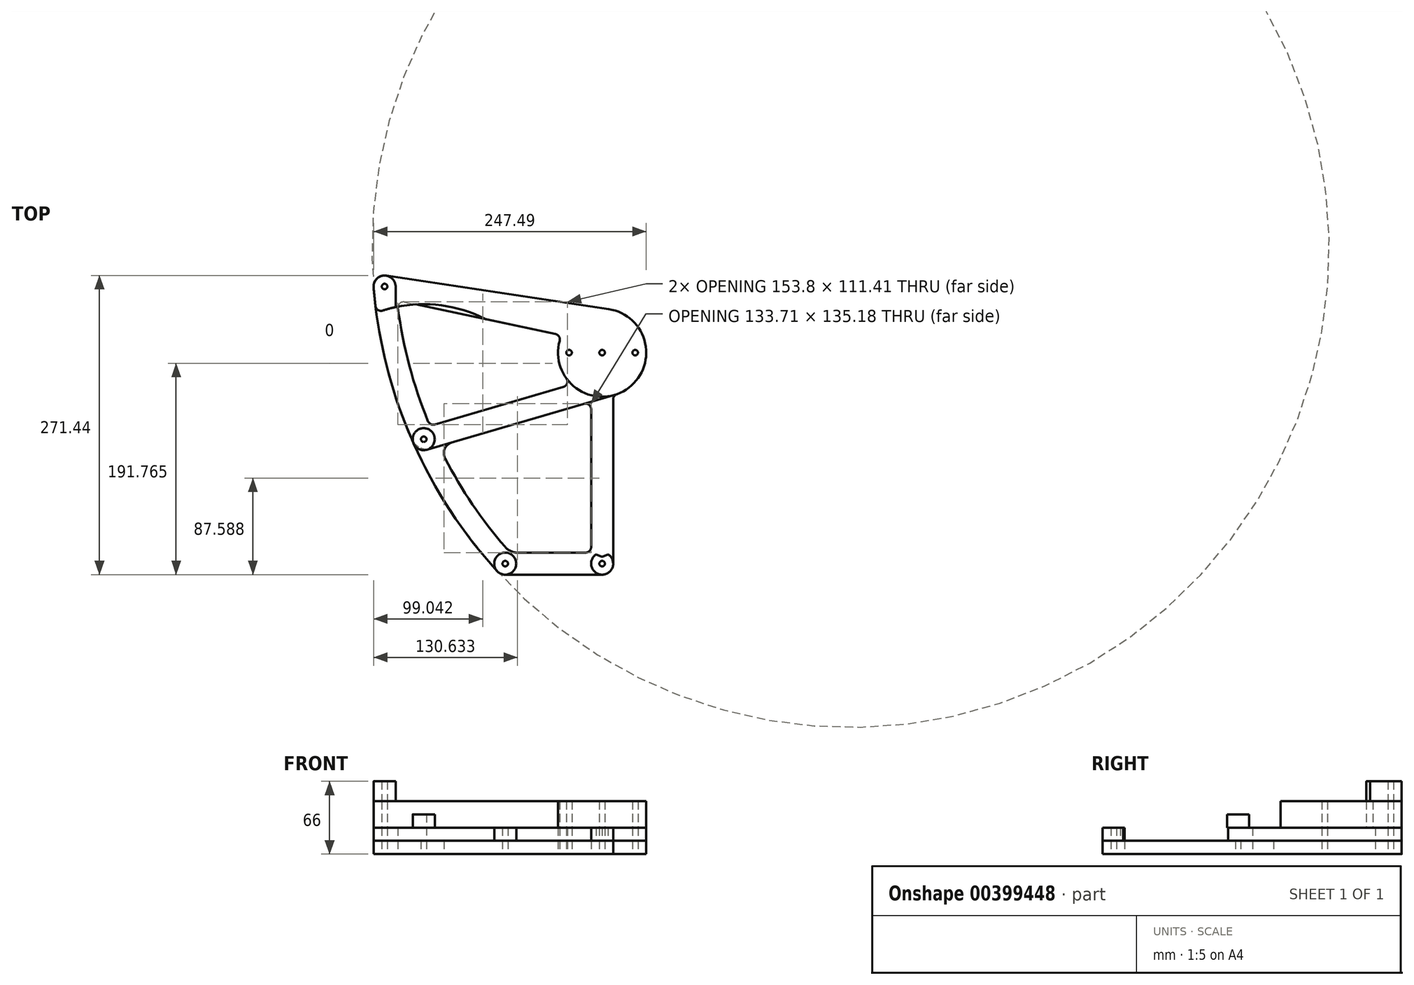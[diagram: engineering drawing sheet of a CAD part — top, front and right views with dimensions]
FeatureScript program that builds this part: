
annotation { "Feature Type Name" : "Feature", "Feature Type Description" : "" }
export const myFeature = defineFeature(function(context is Context, id is Id, definition is map)
    precondition{}
    {
        {
            var Q0;
            Q0=qCreatedBy(makeId("Top.planeOp"),FACE);
            var sketch = newSketch(context, id + "F0", { "sketchPlane" : qUnion([Q0])});
            skArc(sketch, "E0", {"start": v(-38.57, 10.6) * mm, "mid": v(-39.37, -7.07) * mm, "end": v(-32.47, -23.36) * mm});
            skCircle(sketch, "E1", {"center": v(0, 0) * mm, "radius": 2.5 * mm});
            skCircle(sketch, "E2", {"center": v(-30, 0) * mm, "radius": 2.5 * mm});
            skCircle(sketch, "E3", {"center": v(30, 0) * mm, "radius": 2.5 * mm});
            skCircle(sketch, "E4", {"center": v(-197.49, 60) * mm, "radius": 2.5 * mm});
            skCircle(sketch, "E5", {"center": v(-161.97, -78.52) * mm, "radius": 2.5 * mm});
            skCircle(sketch, "E6", {"center": v(-88, -191.44) * mm, "radius": 2.5 * mm});
            skCircle(sketch, "E7", {"center": v(0, -191.44) * mm, "radius": 2.5 * mm});
            skCircle(sketch, "E8", {"center": v(-197.49, 60) * mm, "radius": 10 * mm, "construction": true});
            skCircle(sketch, "E9", {"center": v(-161.97, -78.52) * mm, "radius": 10 * mm, "construction": true});
            skCircle(sketch, "E10", {"center": v(-88, -191.44) * mm, "radius": 10 * mm, "construction": true});
            skArc(sketch, "E11", {"start": v(0, -201.44) * mm, "mid": v(7.07, -198.51) * mm, "end": v(10, -191.44) * mm});
            skLineSegment(sketch, "E12", {"start": v(-196, 69.89) * mm, "end": v(5.94, 39.56) * mm});
            skLineSegment(sketch, "E13", {"start": v(-88, -201.44) * mm, "end": v(0, -201.44) * mm});
            skLineSegment(sketch, "E14", {"start": v(10, -191.44) * mm, "end": v(10, -42.43) * mm});
            skLineSegment(sketch, "E15", {"start": v(-10, -51.25) * mm, "end": v(-10, -176.44) * mm});
            skLineSegment(sketch, "E16", {"start": v(-15, -181.44) * mm, "end": v(-76.76, -181.44) * mm});
            skArc(sketch, "E17", {"start": v(-207.45, 59.18) * mm, "mid": v(-172.78, -78.8) * mm, "end": v(-95.38, -198.18) * mm});
            skPoint(sketch, "E17.first.point", {"position": v(-207.45, 59.18) * mm});
            skPoint(sketch, "E17.second.point", {"position": v(-171.1, -82.6) * mm});
            skPoint(sketch, "E17.third.point", {"position": v(-95.38, -198.18) * mm});
            skArc(sketch, "E18", {"start": v(-185.33, 40.38) * mm, "mid": v(-175, -11.84) * mm, "end": v(-158.04, -62.29) * mm});
            skPoint(sketch, "E18.first.point", {"position": v(-188.38, 55.87) * mm});
            skPoint(sketch, "E18.second.point", {"position": v(-152.84, -74.44) * mm});
            skPoint(sketch, "E18.third.point", {"position": v(-85.08, -181.88) * mm});
            skLineSegment(sketch, "E19", {"start": v(-179.34, 45.92) * mm, "end": v(-42.35, 16.82) * mm});
            skLineSegment(sketch, "E20", {"start": v(-136.52, -81.5) * mm, "end": v(-16.4, -46.45) * mm});
            skLineSegment(sketch, "E21", {"start": v(-152.01, -65.2) * mm, "end": v(-35.12, -31.08) * mm});
            skArc(sketch, "E22", {"start": v(-95.38, -198.18) * mm, "mid": v(-92.03, -200.6) * mm, "end": v(-88, -201.44) * mm});
            skArc(sketch, "E23.filletArc", {"start": v(-88.1, -176.25) * mm, "mid": v(-83, -180.08) * mm, "end": v(-76.76, -181.44) * mm});
            skArc(sketch, "E24.trimOffspring", {"start": v(-142.6, -95.7) * mm, "mid": v(-117.73, -137.58) * mm, "end": v(-88.1, -176.25) * mm});
            skArc(sketch, "E25.filletArc", {"start": v(-158.04, -62.29) * mm, "mid": v(-155.58, -64.9) * mm, "end": v(-152.01, -65.2) * mm});
            skArc(sketch, "E26.filletArc", {"start": v(-136.52, -81.5) * mm, "mid": v(-142.91, -87.17) * mm, "end": v(-142.6, -95.7) * mm});
            skArc(sketch, "E27.filletArc", {"start": v(-179.34, 45.92) * mm, "mid": v(-183.77, 44.7) * mm, "end": v(-185.33, 40.38) * mm});
            skArc(sketch, "E28.trimOffspring", {"start": v(13.33, -37.71) * mm, "mid": v(39.82, 3.8) * mm, "end": v(5.94, 39.56) * mm});
            skPoint(sketch, "E29.visualSharp", {"position": v(-36.81, 15.64) * mm});
            skArc(sketch, "E29.filletArc", {"start": v(-38.57, 10.6) * mm, "mid": v(-39.12, 14.53) * mm, "end": v(-42.35, 16.82) * mm});
            skPoint(sketch, "E30.visualSharp", {"position": v(-27.65, -28.9) * mm});
            skArc(sketch, "E30.filletArc", {"start": v(-35.12, -31.08) * mm, "mid": v(-31.8, -27.91) * mm, "end": v(-32.47, -23.36) * mm});
            skPoint(sketch, "E31.visualSharp", {"position": v(10, -38.73) * mm});
            skArc(sketch, "E31.filletArc", {"start": v(13.33, -37.71) * mm, "mid": v(10.92, -39.54) * mm, "end": v(10, -42.43) * mm});
            skPoint(sketch, "E32.newPointB", {"position": v(0, -41.67) * mm});
            skArc(sketch, "E32.filletArc", {"start": v(-10, -51.25) * mm, "mid": v(-12, -47.25) * mm, "end": v(-16.4, -46.45) * mm});
            skArc(sketch, "E33", {"start": v(-207.45, 59.18) * mm, "mid": v(-204.32, 67.3) * mm, "end": v(-196, 69.89) * mm});
            skPoint(sketch, "E34.visualSharp", {"position": v(-10, -181.44) * mm});
            skArc(sketch, "E34.filletArc", {"start": v(-15, -181.44) * mm, "mid": v(-11.46, -179.98) * mm, "end": v(-10, -176.44) * mm});
            skSolve(sketch);
        }
        {
            var Q0;
            Q0=makeQuery(id+"F0.imprint","IMPRINT",FACE,{"disambiguationData":[TD([[makeQuery(id+"F0.imprint","IMPRINT",EDGE,{"derivedFrom":sQuery(id+"F0.wireOp",EDGE,"E0")}),1.0]])]});
            extrude(context, id + "F1", {"entities" : qUnion([Q0]), "depth" : 12 * mm});
        }
        {
            var Q0;
            Q0=makeQuery(id+"F1.opExtrude","CAP_FACE",FACE,{"disambiguationData":[OSD([sQuery(id+"F0.wireOp",EDGE,"E0"),sQuery(id+"F0.wireOp",EDGE,"E1"),sQuery(id+"F0.wireOp",EDGE,"E2"),sQuery(id+"F0.wireOp",EDGE,"E3"),sQuery(id+"F0.wireOp",EDGE,"E4"),sQuery(id+"F0.wireOp",EDGE,"E5"),sQuery(id+"F0.wireOp",EDGE,"E6"),sQuery(id+"F0.wireOp",EDGE,"E7"),sQuery(id+"F0.wireOp",EDGE,"E11"),sQuery(id+"F0.wireOp",EDGE,"E12"),sQuery(id+"F0.wireOp",EDGE,"E13"),sQuery(id+"F0.wireOp",EDGE,"E14"),sQuery(id+"F0.wireOp",EDGE,"E15"),sQuery(id+"F0.wireOp",EDGE,"E16"),sQuery(id+"F0.wireOp",EDGE,"E17"),sQuery(id+"F0.wireOp",EDGE,"E18"),sQuery(id+"F0.wireOp",EDGE,"E19"),sQuery(id+"F0.wireOp",EDGE,"E20"),sQuery(id+"F0.wireOp",EDGE,"E21"),sQuery(id+"F0.wireOp",EDGE,"E22"),sQuery(id+"F0.wireOp",EDGE,"E23.filletArc"),sQuery(id+"F0.wireOp",EDGE,"E24.trimOffspring"),sQuery(id+"F0.wireOp",EDGE,"E25.filletArc"),sQuery(id+"F0.wireOp",EDGE,"E26.filletArc"),sQuery(id+"F0.wireOp",EDGE,"E27.filletArc"),sQuery(id+"F0.wireOp",EDGE,"E28.trimOffspring"),sQuery(id+"F0.wireOp",EDGE,"E29.filletArc"),sQuery(id+"F0.wireOp",EDGE,"E30.filletArc"),sQuery(id+"F0.wireOp",EDGE,"E31.filletArc"),sQuery(id+"F0.wireOp",EDGE,"E32.filletArc"),sQuery(id+"F0.wireOp",EDGE,"E33"),sQuery(id+"F0.wireOp",EDGE,"E34.filletArc")])],"isStart":false});
            var sketch = newSketch(context, id + "F2", { "sketchPlane" : qUnion([Q0])});
            skArc(sketch, "E35.0", {"start": v(-207.45, 59.18) * mm, "mid": v(-204.32, 67.3) * mm, "end": v(-196, 69.89) * mm});
            skLineSegment(sketch, "E35.1", {"start": v(-196, 69.89) * mm, "end": v(5.94, 39.56) * mm});
            skArc(sketch, "E35.2", {"start": v(-207.45, 59.18) * mm, "mid": v(-195.85, -11.06) * mm, "end": v(-172.92, -78.47) * mm});
            skLineSegment(sketch, "E35.3", {"start": v(-154.96, -86.9) * mm, "end": v(11.2, -38.4) * mm});
            skArc(sketch, "E35.4", {"start": v(11.2, -38.4) * mm, "mid": v(39.9, 2.7) * mm, "end": v(5.94, 39.56) * mm});
            skPoint(sketch, "E36.orphan", {"position": v(-136.52, -81.5) * mm});
            skPoint(sketch, "E37.orphan", {"position": v(-16.4, -46.45) * mm});
            skPoint(sketch, "E38.orphan", {"position": v(13.33, -37.71) * mm});
            skPoint(sketch, "E39.orphan", {"position": v(-95.38, -198.18) * mm});
            skPoint(sketch, "E40.visualSharp", {"position": v(-167.46, -90.54) * mm});
            skArc(sketch, "E40.filletArc", {"start": v(-172.92, -78.47) * mm, "mid": v(-165.53, -86.07) * mm, "end": v(-154.96, -86.9) * mm});
            skArc(sketch, "E41.0", {"start": v(-185.33, 40.38) * mm, "mid": v(-175, -11.84) * mm, "end": v(-158.04, -62.29) * mm});
            skArc(sketch, "E41.1", {"start": v(-179.34, 45.92) * mm, "mid": v(-183.77, 44.7) * mm, "end": v(-185.33, 40.38) * mm});
            skLineSegment(sketch, "E41.2", {"start": v(-179.34, 45.92) * mm, "end": v(-42.35, 16.82) * mm});
            skArc(sketch, "E41.3", {"start": v(-38.57, 10.6) * mm, "mid": v(-39.12, 14.53) * mm, "end": v(-42.35, 16.82) * mm});
            skArc(sketch, "E41.4", {"start": v(-38.57, 10.6) * mm, "mid": v(-39.37, -7.07) * mm, "end": v(-32.47, -23.36) * mm});
            skArc(sketch, "E41.5", {"start": v(-35.12, -31.08) * mm, "mid": v(-31.8, -27.91) * mm, "end": v(-32.47, -23.36) * mm});
            skLineSegment(sketch, "E41.6", {"start": v(-152.01, -65.2) * mm, "end": v(-35.12, -31.08) * mm});
            skArc(sketch, "E41.7", {"start": v(-158.04, -62.29) * mm, "mid": v(-155.58, -64.9) * mm, "end": v(-152.01, -65.2) * mm});
            skCircle(sketch, "E42.0", {"center": v(-197.49, 60) * mm, "radius": 2.5 * mm});
            skCircle(sketch, "E43.1", {"center": v(-161.97, -78.52) * mm, "radius": 2.5 * mm});
            skCircle(sketch, "E44.0", {"center": v(30, 0) * mm, "radius": 2.5 * mm});
            skCircle(sketch, "E45.0", {"center": v(-30, 0) * mm, "radius": 2.5 * mm});
            skCircle(sketch, "E45.1", {"center": v(0, 0) * mm, "radius": 2.5 * mm});
            skSolve(sketch);
        }
        {
            var Q0;
            Q0 = qSketchRegion(id + "F2", true);
            extrude(context, id + "F3", {"entities" : qUnion([Q0]), "depth" : 12 * mm});
        }
        {
            var Q0;
            Q0=makeQuery(id+"F3.opExtrude","CAP_FACE",FACE,{"disambiguationData":[OSD([sQuery(id+"F2.wireOp",EDGE,"E35.0"),sQuery(id+"F2.wireOp",EDGE,"E35.1"),sQuery(id+"F2.wireOp",EDGE,"E35.2"),sQuery(id+"F2.wireOp",EDGE,"E35.3"),sQuery(id+"F2.wireOp",EDGE,"E35.4"),sQuery(id+"F2.wireOp",EDGE,"E40.filletArc"),sQuery(id+"F2.wireOp",EDGE,"E41.0"),sQuery(id+"F2.wireOp",EDGE,"E41.1"),sQuery(id+"F2.wireOp",EDGE,"E41.2"),sQuery(id+"F2.wireOp",EDGE,"E41.3"),sQuery(id+"F2.wireOp",EDGE,"E41.4"),sQuery(id+"F2.wireOp",EDGE,"E41.5"),sQuery(id+"F2.wireOp",EDGE,"E41.6"),sQuery(id+"F2.wireOp",EDGE,"E41.7"),sQuery(id+"F2.wireOp",EDGE,"E42.0"),sQuery(id+"F2.wireOp",EDGE,"E43.1"),sQuery(id+"F2.wireOp",EDGE,"E44.0"),sQuery(id+"F2.wireOp",EDGE,"E45.0"),sQuery(id+"F2.wireOp",EDGE,"E45.1")])],"isStart":false});
            var sketch = newSketch(context, id + "F4", { "sketchPlane" : qUnion([Q0])});
            skCircle(sketch, "E46.0", {"center": v(-161.97, -78.52) * mm, "radius": 2.5 * mm, "construction": true});
            skArc(sketch, "E47", {"start": v(-106.23, 30.57) * mm, "mid": v(-152, 43.57) * mm, "end": v(-199.26, 38.17) * mm});
            skArc(sketch, "E48.0", {"start": v(-207.45, 59.18) * mm, "mid": v(-204.32, 67.3) * mm, "end": v(-196, 69.89) * mm});
            skArc(sketch, "E48.1", {"start": v(-207.45, 59.18) * mm, "mid": v(-206.68, 50.75) * mm, "end": v(-205.74, 42.33) * mm});
            skLineSegment(sketch, "E49.0", {"start": v(-196, 69.89) * mm, "end": v(5.94, 39.56) * mm});
            skArc(sketch, "E50.converted", {"start": v(-38.57, 10.6) * mm, "mid": v(21.81, -33.53) * mm, "end": v(5.94, 39.56) * mm});
            skPoint(sketch, "E51.orphan", {"position": v(11.2, -38.4) * mm});
            skLineSegment(sketch, "E52.0", {"start": v(-105, 30.13) * mm, "end": v(-42.35, 16.82) * mm});
            skArc(sketch, "E53.0", {"start": v(-38.57, 10.6) * mm, "mid": v(-39.12, 14.53) * mm, "end": v(-42.35, 16.82) * mm});
            skPoint(sketch, "E54.orphan", {"position": v(-172.92, -78.47) * mm});
            skPoint(sketch, "E55.orphan", {"position": v(-179.34, 45.92) * mm});
            skCircle(sketch, "E56.0", {"center": v(-30, 0) * mm, "radius": 2.5 * mm});
            skCircle(sketch, "E56.1", {"center": v(0, 0) * mm, "radius": 2.5 * mm});
            skCircle(sketch, "E56.2", {"center": v(30, 0) * mm, "radius": 2.5 * mm});
            skPoint(sketch, "E57.visualSharp", {"position": v(-204.95, 36.2) * mm});
            skArc(sketch, "E57.filletArc", {"start": v(-205.74, 42.33) * mm, "mid": v(-203.48, 38.72) * mm, "end": v(-199.26, 38.17) * mm});
            skPoint(sketch, "E58.visualSharp", {"position": v(-105.65, 30.27) * mm});
            skArc(sketch, "E58.filletArc", {"start": v(-106.23, 30.57) * mm, "mid": v(-105.63, 30.3) * mm, "end": v(-105, 30.13) * mm});
            skCircle(sketch, "E59.0", {"center": v(-197.49, 60) * mm, "radius": 2.5 * mm});
            skSolve(sketch);
        }
        {
            var Q0;
            Q0 = qSketchRegion(id + "F4", true);
            extrude(context, id + "F5", {"entities" : qUnion([Q0]), "depth" : 24 * mm});
        }
        {
            var Q0;
            Q0=makeQuery(id+"F1.opExtrude","CAP_FACE",FACE,{"disambiguationData":[OSD([sQuery(id+"F0.wireOp",EDGE,"E0"),sQuery(id+"F0.wireOp",EDGE,"E1"),sQuery(id+"F0.wireOp",EDGE,"E2"),sQuery(id+"F0.wireOp",EDGE,"E3"),sQuery(id+"F0.wireOp",EDGE,"E4"),sQuery(id+"F0.wireOp",EDGE,"E5"),sQuery(id+"F0.wireOp",EDGE,"E6"),sQuery(id+"F0.wireOp",EDGE,"E7"),sQuery(id+"F0.wireOp",EDGE,"E11"),sQuery(id+"F0.wireOp",EDGE,"E12"),sQuery(id+"F0.wireOp",EDGE,"E13"),sQuery(id+"F0.wireOp",EDGE,"E14"),sQuery(id+"F0.wireOp",EDGE,"E15"),sQuery(id+"F0.wireOp",EDGE,"E16"),sQuery(id+"F0.wireOp",EDGE,"E17"),sQuery(id+"F0.wireOp",EDGE,"E18"),sQuery(id+"F0.wireOp",EDGE,"E19"),sQuery(id+"F0.wireOp",EDGE,"E20"),sQuery(id+"F0.wireOp",EDGE,"E21"),sQuery(id+"F0.wireOp",EDGE,"E22"),sQuery(id+"F0.wireOp",EDGE,"E23.filletArc"),sQuery(id+"F0.wireOp",EDGE,"E24.trimOffspring"),sQuery(id+"F0.wireOp",EDGE,"E25.filletArc"),sQuery(id+"F0.wireOp",EDGE,"E26.filletArc"),sQuery(id+"F0.wireOp",EDGE,"E27.filletArc"),sQuery(id+"F0.wireOp",EDGE,"E28.trimOffspring"),sQuery(id+"F0.wireOp",EDGE,"E29.filletArc"),sQuery(id+"F0.wireOp",EDGE,"E30.filletArc"),sQuery(id+"F0.wireOp",EDGE,"E31.filletArc"),sQuery(id+"F0.wireOp",EDGE,"E32.filletArc"),sQuery(id+"F0.wireOp",EDGE,"E33"),sQuery(id+"F0.wireOp",EDGE,"E34.filletArc")])],"isStart":false});
            var sketch = newSketch(context, id + "F6", { "sketchPlane" : qUnion([Q0])});
            skCircle(sketch, "E60.0", {"center": v(-88, -191.44) * mm, "radius": 2.5 * mm});
            skCircle(sketch, "E60.1", {"center": v(0, -191.44) * mm, "radius": 2.5 * mm});
            skArc(sketch, "E61", {"start": v(-5.3, -182.97) * mm, "mid": v(0, -201.44) * mm, "end": v(5.3, -182.97) * mm});
            skCircle(sketch, "E62", {"center": v(-88, -191.44) * mm, "radius": 10 * mm});
            skLineSegment(sketch, "E63", {"start": v(0, -191.44) * mm, "end": v(0, -113.22) * mm, "construction": true});
            skLineSegment(sketch, "E64", {"start": v(-5.3, -182.97) * mm, "end": v(0, -185.44) * mm});
            skLineSegment(sketch, "E65", {"start": v(0, -185.44) * mm, "end": v(5.3, -182.97) * mm});
            skSolve(sketch);
        }
        {
            var Q0;
            Q0 = qSketchRegion(id + "F6", true);
            extrude(context, id + "F7", {"entities" : qUnion([Q0]), "depth" : 12 * mm});
        }
        {
            var Q0;
            Q0=makeQuery(id+"F5.opExtrude","CAP_FACE",FACE,{"disambiguationData":[OSD([sQuery(id+"F4.wireOp",EDGE,"E47"),sQuery(id+"F4.wireOp",EDGE,"E48.0"),sQuery(id+"F4.wireOp",EDGE,"E48.1"),sQuery(id+"F4.wireOp",EDGE,"E49.0"),sQuery(id+"F4.wireOp",EDGE,"E50.converted"),sQuery(id+"F4.wireOp",EDGE,"E52.0"),sQuery(id+"F4.wireOp",EDGE,"E53.0"),sQuery(id+"F4.wireOp",EDGE,"E56.0"),sQuery(id+"F4.wireOp",EDGE,"E56.1"),sQuery(id+"F4.wireOp",EDGE,"E56.2"),sQuery(id+"F4.wireOp",EDGE,"E57.filletArc"),sQuery(id+"F4.wireOp",EDGE,"E58.filletArc"),sQuery(id+"F4.wireOp",EDGE,"E59.0")])],"isStart":false});
            var sketch = newSketch(context, id + "F8", { "sketchPlane" : qUnion([Q0])});
            skCircle(sketch, "E66.0", {"center": v(-197.49, 60) * mm, "radius": 2.5 * mm});
            skArc(sketch, "E67.0", {"start": v(-207.45, 59.18) * mm, "mid": v(-197.94, 69.99) * mm, "end": v(-187.49, 60.09) * mm});
            skArc(sketch, "E68.0", {"start": v(-207.45, 59.18) * mm, "mid": v(-206.68, 50.75) * mm, "end": v(-205.74, 42.33) * mm});
            skArc(sketch, "E69.0", {"start": v(-205.74, 42.33) * mm, "mid": v(-203.48, 38.72) * mm, "end": v(-199.26, 38.17) * mm});
            skArc(sketch, "E70.0", {"start": v(-187.49, 41.3) * mm, "mid": v(-193.41, 39.88) * mm, "end": v(-199.26, 38.17) * mm});
            skPoint(sketch, "E71.orphan", {"position": v(-196, 69.89) * mm});
            skPoint(sketch, "E72.orphan", {"position": v(-106.23, 30.57) * mm});
            skLineSegment(sketch, "E73", {"start": v(-187.49, 60.09) * mm, "end": v(-187.49, 41.3) * mm});
            skSolve(sketch);
        }
        {
            var Q0;
            Q0 = qSketchRegion(id + "F8", true);
            extrude(context, id + "F9", {"entities" : qUnion([Q0]), "depth" : 18 * mm});
        }
        {
            var Q0;
            Q0=makeQuery(id+"F3.opExtrude","CAP_FACE",FACE,{"disambiguationData":[OSD([sQuery(id+"F2.wireOp",EDGE,"E35.0"),sQuery(id+"F2.wireOp",EDGE,"E35.1"),sQuery(id+"F2.wireOp",EDGE,"E35.2"),sQuery(id+"F2.wireOp",EDGE,"E35.3"),sQuery(id+"F2.wireOp",EDGE,"E35.4"),sQuery(id+"F2.wireOp",EDGE,"E40.filletArc"),sQuery(id+"F2.wireOp",EDGE,"E41.0"),sQuery(id+"F2.wireOp",EDGE,"E41.1"),sQuery(id+"F2.wireOp",EDGE,"E41.2"),sQuery(id+"F2.wireOp",EDGE,"E41.3"),sQuery(id+"F2.wireOp",EDGE,"E41.4"),sQuery(id+"F2.wireOp",EDGE,"E41.5"),sQuery(id+"F2.wireOp",EDGE,"E41.6"),sQuery(id+"F2.wireOp",EDGE,"E41.7"),sQuery(id+"F2.wireOp",EDGE,"E42.0"),sQuery(id+"F2.wireOp",EDGE,"E43.1"),sQuery(id+"F2.wireOp",EDGE,"E44.0"),sQuery(id+"F2.wireOp",EDGE,"E45.0"),sQuery(id+"F2.wireOp",EDGE,"E45.1")])],"isStart":false});
            var sketch = newSketch(context, id + "F10", { "sketchPlane" : qUnion([Q0])});
            skCircle(sketch, "E74.0", {"center": v(-161.97, -78.52) * mm, "radius": 2.5 * mm});
            skCircle(sketch, "E75", {"center": v(-161.97, -78.52) * mm, "radius": 10 * mm});
            skSolve(sketch);
        }
        {
            var Q0;
            Q0 = qSketchRegion(id + "F10", true);
            extrude(context, id + "F11", {"entities" : qUnion([Q0]), "operationType" : NewBodyOperationType.ADD, "depth" : 12 * mm});
        }
    });
